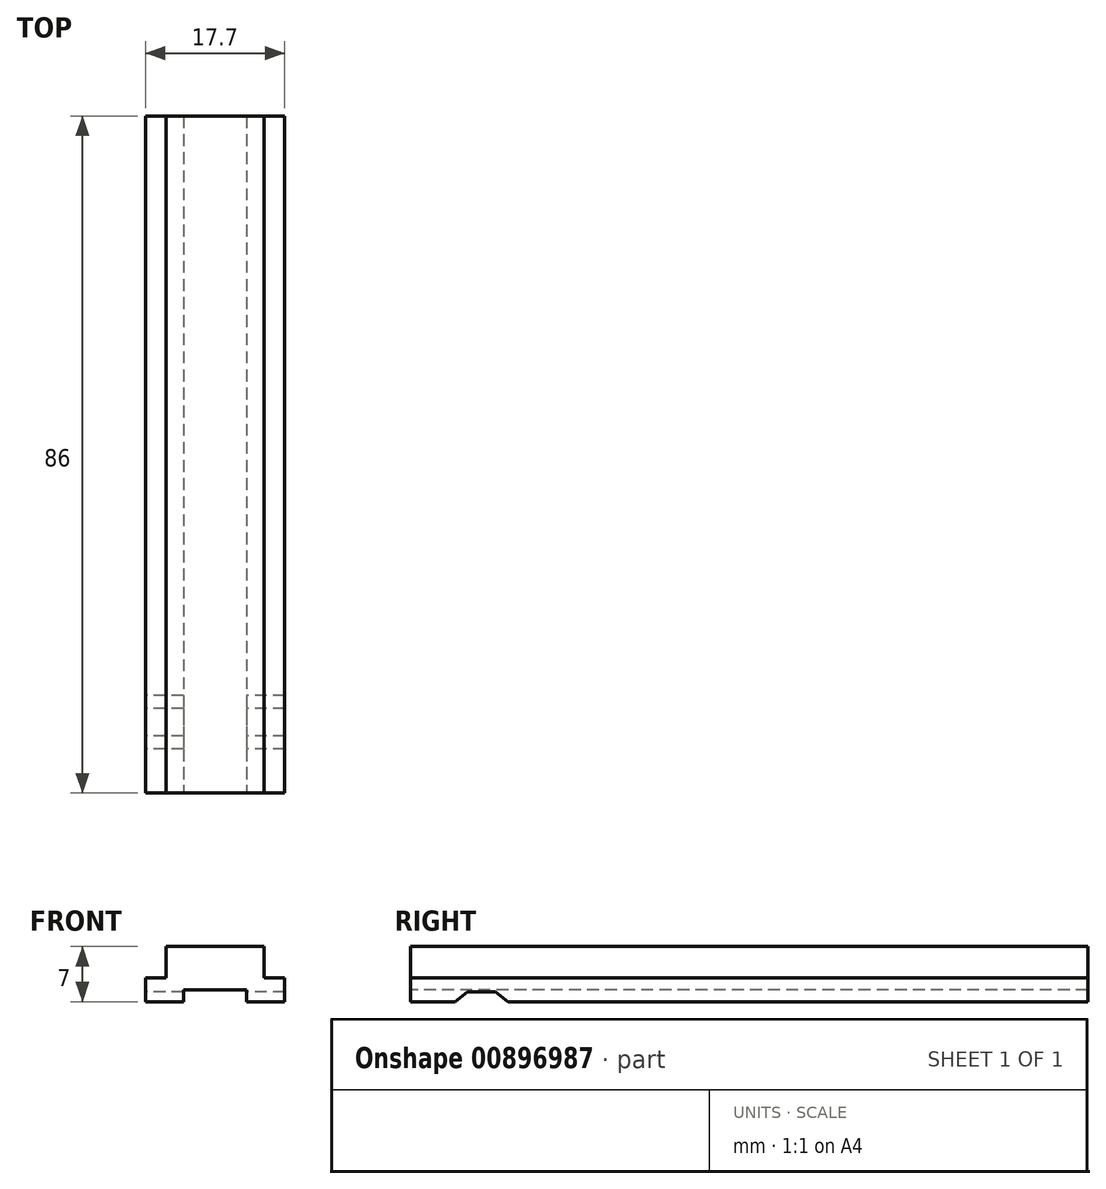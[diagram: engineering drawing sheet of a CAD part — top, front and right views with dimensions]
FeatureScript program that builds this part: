
annotation { "Feature Type Name" : "Feature", "Feature Type Description" : "" }
export const myFeature = defineFeature(function(context is Context, id is Id, definition is map)
    precondition{}
    {
        {
            var Q0;
            Q0=qCreatedBy(makeId("Top.planeOp"),FACE);
            var sketch = newSketch(context, id + "F0", { "sketchPlane" : qUnion([Q0])});
            skLineSegment(sketch, "E0.bottom", {"start": v(-14.02, 133.71) * mm, "end": v(3.68, 133.71) * mm});
            skLineSegment(sketch, "E0.top", {"start": v(-14.02, 47.71) * mm, "end": v(3.68, 47.71) * mm});
            skLineSegment(sketch, "E0.left", {"start": v(-14.02, 133.71) * mm, "end": v(-14.02, 47.71) * mm});
            skLineSegment(sketch, "E0.right", {"start": v(3.68, 133.71) * mm, "end": v(3.68, 47.71) * mm});
            skSolve(sketch);
        }
        {
            var Q0;
            Q0 = qSketchRegion(id + "F0", true);
            var Q1;
            Q1=makeQuery(id+"F0.imprint","IMPRINT",FACE,{"disambiguationData":[TD([[makeQuery(id+"F0.imprint","IMPRINT",EDGE,{"derivedFrom":sQuery(id+"F0.wireOp",EDGE,"E0.bottom")}),-1.0]])]});
            extrude(context, id + "F1", {"entities" : qUnion([Q0, Q1]), "depth" : 3 * mm, "offsetDistance" : 25 * mm});
        }
        {
            var Q0;
            Q0=makeQuery(id+"F1.opExtrude","CAP_FACE",FACE,{"disambiguationData":[OSD([sQuery(id+"F0.wireOp",EDGE,"E0.bottom"),sQuery(id+"F0.wireOp",EDGE,"E0.top"),sQuery(id+"F0.wireOp",EDGE,"E0.left"),sQuery(id+"F0.wireOp",EDGE,"E0.right")])],"isStart":false});
            var sketch = newSketch(context, id + "F2", { "sketchPlane" : qUnion([Q0])});
            skLineSegment(sketch, "E1", {"start": v(-5.17, 47.71) * mm, "end": v(-11.42, 47.71) * mm});
            skLineSegment(sketch, "E2", {"start": v(-5.17, 47.71) * mm, "end": v(1.08, 47.71) * mm});
            skLineSegment(sketch, "E3", {"start": v(1.08, 47.71) * mm, "end": v(1.08, 133.71) * mm});
            skLineSegment(sketch, "E4.bottom", {"start": v(-11.42, 47.71) * mm, "end": v(1.08, 47.71) * mm});
            skLineSegment(sketch, "E4.top", {"start": v(-11.42, 133.71) * mm, "end": v(1.08, 133.71) * mm});
            skLineSegment(sketch, "E4.left", {"start": v(-11.42, 47.71) * mm, "end": v(-11.42, 133.71) * mm});
            skPoint(sketch, "E5.start.orphan", {"position": v(-5.17, 133.71) * mm});
            skSolve(sketch);
        }
        {
            var Q0;
            Q0 = qSketchRegion(id + "F2", true);
            extrude(context, id + "F3", {"entities" : qUnion([Q0]), "operationType" : NewBodyOperationType.ADD, "depth" : 4 * mm, "offsetDistance" : 25 * mm});
        }
        {
            var Q0;
            Q0=makeQuery(id+"F3.boolean.opBoolean","MERGE",FACE,{"derivedFrom":[makeQuery(id+"F1.opExtrude","SWEPT_FACE",FACE,{"disambiguationData":[OSD([sQuery(id+"F0.wireOp",EDGE,"E0.top")])]}),makeQuery(id+"F3.opExtrude","SWEPT_FACE",FACE,{"disambiguationData":[OSD([sQuery(id+"F2.wireOp",EDGE,"E4.bottom")])]})]});
            var sketch = newSketch(context, id + "F4", { "sketchPlane" : qUnion([Q0])});
            skLineSegment(sketch, "E6", {"start": v(-5.17, 0) * mm, "end": v(-1.17, 0) * mm});
            skLineSegment(sketch, "E7", {"start": v(-1.17, 0) * mm, "end": v(-9.17, 0) * mm});
            skLineSegment(sketch, "E8", {"start": v(-9.17, 0) * mm, "end": v(-9.17, 1.5) * mm});
            skLineSegment(sketch, "E9.top", {"start": v(-1.17, 1.5) * mm, "end": v(-9.17, 1.5) * mm});
            skLineSegment(sketch, "E9.left", {"start": v(-1.17, 0) * mm, "end": v(-1.17, 1.5) * mm});
            skSolve(sketch);
        }
        {
            var Q0;
            Q0 = qSketchRegion(id + "F4", true);
            extrude(context, id + "F5", {"entities" : qUnion([Q0]), "operationType" : NewBodyOperationType.REMOVE, "oppositeDirection" : true, "depth" : 86 * mm, "offsetDistance" : 25 * mm});
        }
        {
            var Q0;
            Q0=makeQuery(id+"F1.opExtrude","SWEPT_FACE",FACE,{"disambiguationData":[OSD([sQuery(id+"F0.wireOp",EDGE,"E0.left")])]});
            var sketch = newSketch(context, id + "F6", { "sketchPlane" : qUnion([Q0])});
            skLineSegment(sketch, "E10", {"start": v(-53.35, 0) * mm, "end": v(-54.95, 1.24) * mm});
            skLineSegment(sketch, "E11", {"start": v(-54.95, 1.24) * mm, "end": v(-58.47, 1.24) * mm});
            skLineSegment(sketch, "E12", {"start": v(-58.47, 1.24) * mm, "end": v(-60.08, 0) * mm});
            skSolve(sketch);
        }
        {
            var Q0;
            Q0 = qSketchRegion(id + "F6", true);
            var Q1;
            {var subQ0=sQuery(id+"F6.wireOp",EDGE,"E10");Q1=makeQuery(id+"F6.imprint","IMPRINT",FACE,{"disambiguationData":[TD([[makeQuery(id+"F6.imprint","IMPRINT",EDGE,{"derivedFrom":subQ0}),1.0]])]});}
            extrude(context, id + "F7", {"entities" : qUnion([Q0, Q1]), "operationType" : NewBodyOperationType.REMOVE, "oppositeDirection" : true, "depth" : 25 * mm, "offsetDistance" : 25 * mm});
        }
    });
